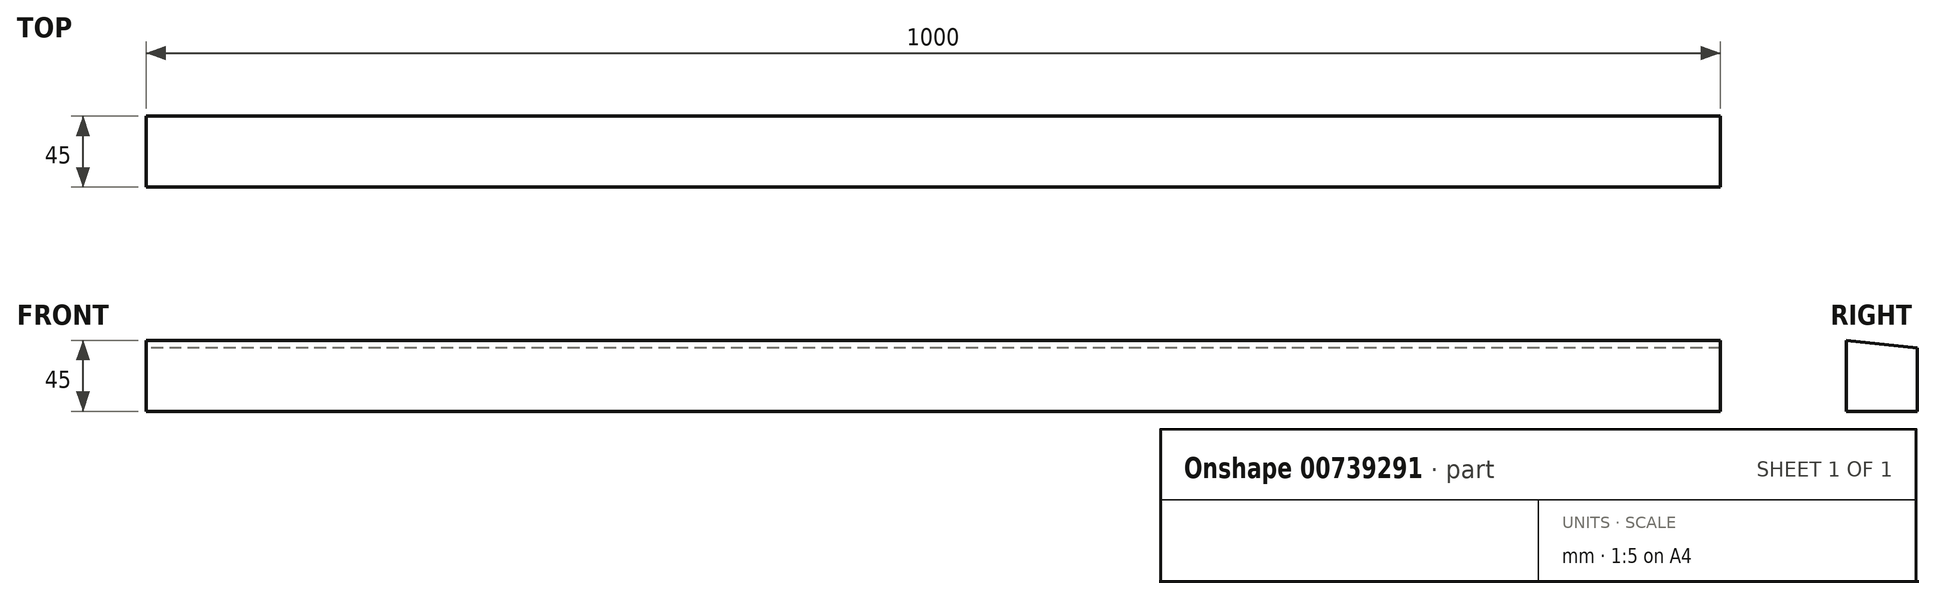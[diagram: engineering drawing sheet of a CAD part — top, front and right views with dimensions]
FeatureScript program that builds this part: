
annotation { "Feature Type Name" : "Feature", "Feature Type Description" : "" }
export const myFeature = defineFeature(function(context is Context, id is Id, definition is map)
    precondition{}
    {
        {
            var Q0;
            Q0=qCreatedBy(makeId("Right.planeOp"),FACE);
            var sketch = newSketch(context, id + "F0", { "sketchPlane" : qUnion([Q0])});
            skLineSegment(sketch, "E0", {"start": v(0, 45) * mm, "end": v(0, 0) * mm});
            skLineSegment(sketch, "E1", {"start": v(0, 0) * mm, "end": v(45, 0) * mm});
            skLineSegment(sketch, "E2", {"start": v(45, 0) * mm, "end": v(45, 40.27) * mm});
            skLineSegment(sketch, "E3", {"start": v(45, 40.27) * mm, "end": v(0, 45) * mm});
            skSolve(sketch);
        }
        {
            var Q0;
            Q0=makeQuery(id+"F0.imprint","IMPRINT",FACE,{"disambiguationData":[TD([[makeQuery(id+"F0.imprint","IMPRINT",EDGE,{"derivedFrom":sQuery(id+"F0.wireOp",EDGE,"E0")}),1.0]])]});
            extrude(context, id + "F1", {"entities" : qUnion([Q0]), "depth" : 1000 * mm, "offsetDistance" : 25 * mm});
        }
    });
